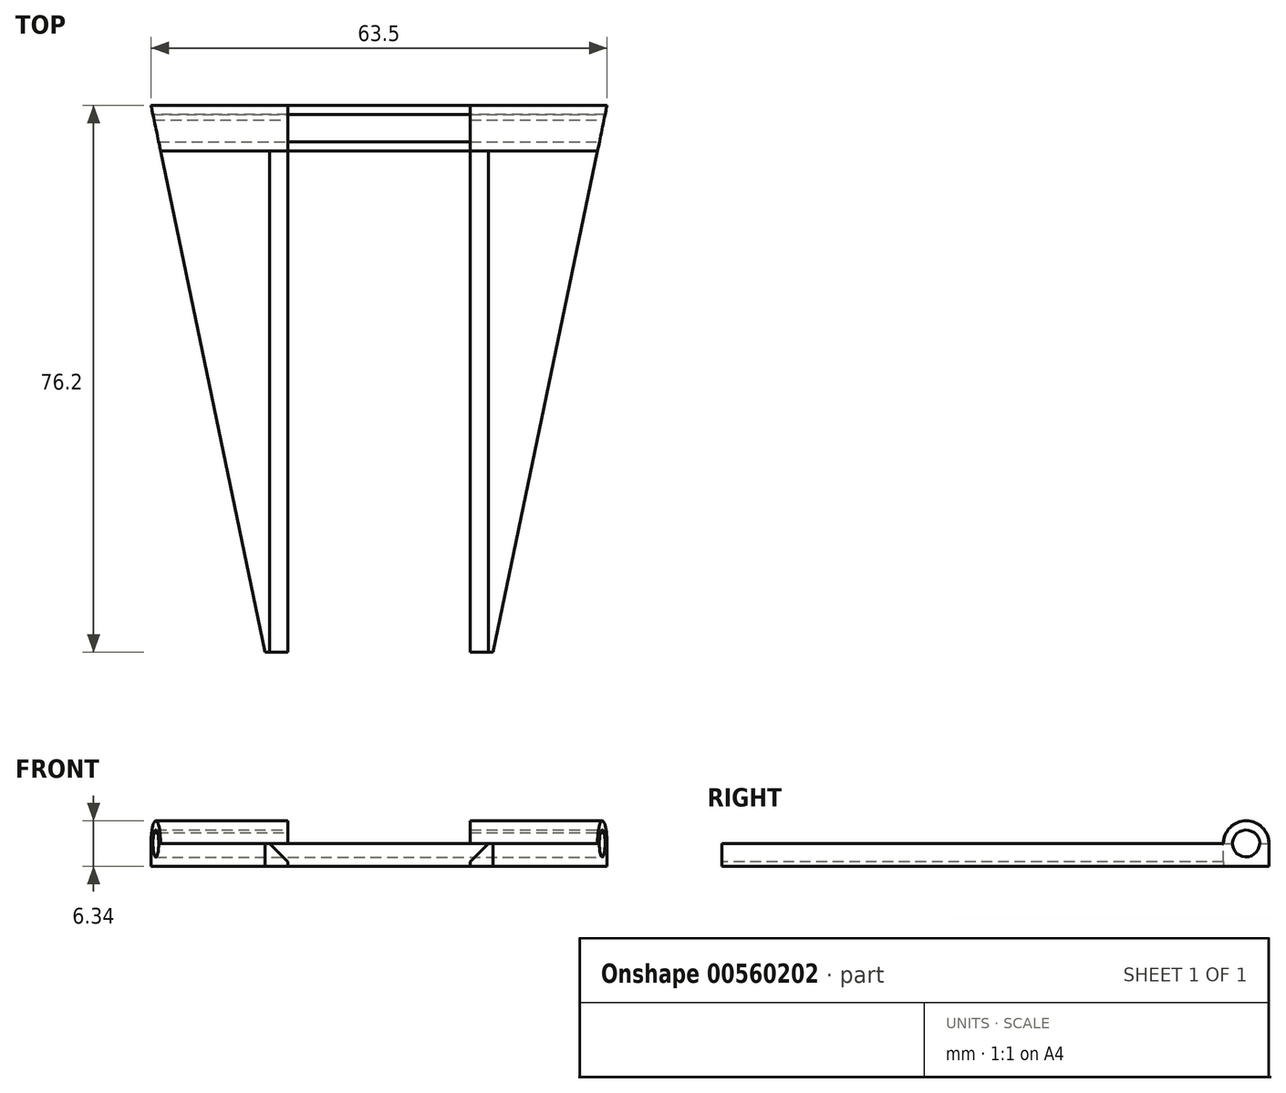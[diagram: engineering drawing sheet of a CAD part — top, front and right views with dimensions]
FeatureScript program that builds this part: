
annotation { "Feature Type Name" : "Feature", "Feature Type Description" : "" }
export const myFeature = defineFeature(function(context is Context, id is Id, definition is map)
    precondition{}
    {
        {
            var Q0;
            Q0=qCreatedBy(makeId("Top.planeOp"),FACE);
            var sketch = newSketch(context, id + "F0", { "sketchPlane" : qUnion([Q0])});
            skLineSegment(sketch, "E0", {"start": v(0, 0) * mm, "end": v(-38.1, 0) * mm});
            skLineSegment(sketch, "E1.MirrorCS", {"start": v(0, 0) * mm, "end": v(38.1, 0) * mm});
            skLineSegment(sketch, "E2", {"start": v(0, -76.2) * mm, "end": v(16.51, -76.2) * mm});
            skLineSegment(sketch, "E3.MirrorCS", {"start": v(0, -76.2) * mm, "end": v(-16.5, -76.2) * mm});
            skLineSegment(sketch, "E4", {"start": v(0, 0) * mm, "end": v(0, -76.2) * mm, "construction": true});
            skLineSegment(sketch, "E5", {"start": v(-38.1, 0) * mm, "end": v(-16.5, -76.2) * mm});
            skLineSegment(sketch, "E6", {"start": v(38.1, 0) * mm, "end": v(16.51, -76.2) * mm});
            skSolve(sketch);
        }
        {
            var Q0;
            Q0 = qSketchRegion(id + "F0", true);
            extrude(context, id + "F1", {"entities" : qUnion([Q0]), "depth" : 3.17 * mm, "offsetDistance" : 25.4 * mm});
        }
        {
            var Q0;
            Q0=qCreatedBy(makeId("Right.planeOp"),FACE);
            var sketch = newSketch(context, id + "F2", { "sketchPlane" : qUnion([Q0])});
            skArc(sketch, "E7", {"start": v(0, 3.16) * mm, "mid": v(-3.17, 6.34) * mm, "end": v(-6.35, 3.16) * mm});
            skLineSegment(sketch, "E8", {"start": v(-3.17, 3.16) * mm, "end": v(0, 3.16) * mm, "construction": true});
            skLineSegment(sketch, "E9", {"start": v(0, 3.16) * mm, "end": v(-3.17, 3.16) * mm});
            skLineSegment(sketch, "E10.MirrorCS", {"start": v(-6.35, 3.16) * mm, "end": v(-3.17, 3.16) * mm});
            skPoint(sketch, "E11.start.orphan", {"position": v(-3.17, -0.01) * mm});
            skArc(sketch, "E12.0", {"start": v(-1.27, 3.16) * mm, "mid": v(-3.17, 5.07) * mm, "end": v(-5.08, 3.16) * mm});
            skArc(sketch, "E13.MirrorCS", {"start": v(-1.27, 3.16) * mm, "mid": v(-3.17, 1.26) * mm, "end": v(-5.08, 3.16) * mm});
            skSolve(sketch);
        }
        {
            var Q0;
            {var subQ0=sQuery(id+"F2.wireOp",EDGE,"E7");Q0=makeQuery(id+"F2.imprint","IMPRINT",FACE,{"disambiguationData":[TD([[makeQuery(id+"F2.imprint","IMPRINT",EDGE,{"derivedFrom":subQ0}),1.0]])]});}
            extrude(context, id + "F3", {"entities" : qUnion([Q0]), "operationType" : NewBodyOperationType.ADD, "endBound" : BoundingType.SYMMETRIC, "depth" : 76.2 * mm, "offsetDistance" : 25.4 * mm});
        }
        {
            var Q0;
            Q0=qCreatedBy(makeId("Right.planeOp"),FACE);
            var sketch = newSketch(context, id + "F4", { "sketchPlane" : qUnion([Q0])});
            skCircle(sketch, "E14", {"center": v(-3.2, 3.18) * mm, "radius": 1.9 * mm});
            skSolve(sketch);
        }
        {
            var Q0;
            Q0 = qSketchRegion(id + "F4", true);
            extrude(context, id + "F5", {"entities" : qUnion([Q0]), "operationType" : NewBodyOperationType.REMOVE, "endBound" : BoundingType.SYMMETRIC, "oppositeDirection" : true, "depth" : 76.2 * mm, "offsetDistance" : 25.4 * mm});
        }
        {
            var Q0;
            Q0=qCreatedBy(makeId("Front.planeOp"),FACE);
            var sketch = newSketch(context, id + "F6", { "sketchPlane" : qUnion([Q0])});
            skLineSegment(sketch, "E15", {"start": v(0, 0) * mm, "end": v(0, 3.17) * mm});
            skLineSegment(sketch, "E16", {"start": v(0, 3.17) * mm, "end": v(12.7, 3.17) * mm});
            skLineSegment(sketch, "E17.MirrorCS", {"start": v(0, 3.17) * mm, "end": v(-12.7, 3.17) * mm});
            skLineSegment(sketch, "E18", {"start": v(12.7, 3.17) * mm, "end": v(12.7, 6.35) * mm});
            skLineSegment(sketch, "E19.MirrorCS", {"start": v(-12.7, 3.17) * mm, "end": v(-12.7, 6.35) * mm});
            skLineSegment(sketch, "E20", {"start": v(12.7, 6.35) * mm, "end": v(-12.7, 6.35) * mm});
            skSolve(sketch);
        }
        {
            var Q0;
            Q0 = qSketchRegion(id + "F6", true);
            extrude(context, id + "F7", {"entities" : qUnion([Q0]), "operationType" : NewBodyOperationType.REMOVE, "depth" : 12.7 * mm, "offsetDistance" : 25.4 * mm});
        }
        {
            var Q0;
            Q0=qCreatedBy(makeId("Top.planeOp"),FACE);
            var sketch = newSketch(context, id + "F8", { "sketchPlane" : qUnion([Q0])});
            skLineSegment(sketch, "E21", {"start": v(0, 0) * mm, "end": v(-31.75, 0) * mm});
            skLineSegment(sketch, "E22", {"start": v(-15.88, -76.2) * mm, "end": v(0, -76.2) * mm});
            skLineSegment(sketch, "E23", {"start": v(-31.75, 0) * mm, "end": v(-15.88, -76.2) * mm});
            skLineSegment(sketch, "E24.MirrorCS", {"start": v(15.88, -76.2) * mm, "end": v(0, -76.2) * mm});
            skLineSegment(sketch, "E25.MirrorCS", {"start": v(31.75, 0) * mm, "end": v(15.87, -76.2) * mm});
            skLineSegment(sketch, "E26.MirrorCS", {"start": v(0, 0) * mm, "end": v(31.75, 0) * mm});
            skSolve(sketch);
        }
        {
            var Q0;
            Q0=makeQuery(id+"F8.imprint","IMPRINT",FACE,{"disambiguationData":[TD([[makeQuery(id+"F8.imprint","IMPRINT",EDGE,{"derivedFrom":sQuery(id+"F8.wireOp",EDGE,"E21")}),1.0]])]});
            extrude(context, id + "F9", {"entities" : qUnion([Q0]), "operationType" : NewBodyOperationType.INTERSECT, "depth" : 25.4 * mm, "offsetDistance" : 25.4 * mm});
        }
        {
            var Q0;
            Q0=qCreatedBy(makeId("Right.planeOp"),FACE);
            var sketch = newSketch(context, id + "F10", { "sketchPlane" : qUnion([Q0])});
            skLineSegment(sketch, "E27", {"start": v(-28.96, 5.38) * mm, "end": v(-28.96, 2.84) * mm});
            skLineSegment(sketch, "E28", {"start": v(-28.96, 5.38) * mm, "end": v(-27.65, 5.38) * mm});
            skLineSegment(sketch, "E29", {"start": v(-27.65, 5.38) * mm, "end": v(-27.65, 2.84) * mm});
            skLineSegment(sketch, "E30", {"start": v(-27.65, 2.84) * mm, "end": v(-28.96, 2.84) * mm});
            skSolve(sketch);
        }
        {
            var Q0;
            Q0=makeQuery(id+"F10.imprint","IMPRINT",FACE,{"disambiguationData":[TD([[makeQuery(id+"F10.imprint","IMPRINT",EDGE,{"derivedFrom":sQuery(id+"F10.wireOp",EDGE,"E27")}),1.0]])]});
            extrude(context, id + "F11", {"entities" : qUnion([Q0]), "operationType" : NewBodyOperationType.ADD, "endBound" : BoundingType.SYMMETRIC, "depth" : 12.7 * mm, "offsetDistance" : 25.4 * mm});
        }
        {
            var Q0;
            Q0=qCreatedBy(makeId("Top.planeOp"),FACE);
            var sketch = newSketch(context, id + "F12", { "sketchPlane" : qUnion([Q0])});
            skLineSegment(sketch, "E31", {"start": v(-12.71, -6.35) * mm, "end": v(12.69, -6.35) * mm});
            skLineSegment(sketch, "E32", {"start": v(12.69, -6.35) * mm, "end": v(12.69, -80.87) * mm});
            skLineSegment(sketch, "E33", {"start": v(12.69, -80.87) * mm, "end": v(-12.71, -80.87) * mm});
            skLineSegment(sketch, "E34", {"start": v(-12.71, -6.35) * mm, "end": v(-12.71, -80.87) * mm});
            skSolve(sketch);
        }
        {
            var Q0;
            Q0 = qSketchRegion(id + "F12", true);
            extrude(context, id + "F13", {"entities" : qUnion([Q0]), "operationType" : NewBodyOperationType.REMOVE, "depth" : 12.7 * mm, "offsetDistance" : 25.4 * mm});
        }
        {
            var Q0;
            {var subQ0=sQuery(id+"F0.wireOp",EDGE,"E3.MirrorCS");var subQ1=sQuery(id+"F0.wireOp",EDGE,"E2");var subQ2=sQuery(id+"F0.wireOp",EDGE,"E5");var subQ3=sQuery(id+"F0.wireOp",EDGE,"E6");Q0=makeQuery(id+"F13.boolean.opBoolean","INTERSECT",EDGE,{"derivedFrom":[makeQuery(id+"F7.boolean.opBoolean","MERGE",FACE,{"derivedFrom":[makeQuery(id+"F3.boolean.opBoolean","SPLIT",FACE,{"disambiguationData":[TD([makeQuery(id+"F1.opExtrude","SWEPT_FACE",FACE,{"disambiguationData":[OSD([subQ1,subQ0])]})])],"derivedFrom":makeQuery(id+"F1.opExtrude","CAP_FACE",FACE,{"disambiguationData":[OSD([sQuery(id+"F0.wireOp",EDGE,"E0"),sQuery(id+"F0.wireOp",EDGE,"E1.MirrorCS"),subQ1,subQ0,subQ2,subQ3])],"isStart":false})}),makeQuery(id+"F7.opExtrude","SWEPT_FACE",FACE,{"disambiguationData":[OSD([sQuery(id+"F6.wireOp",EDGE,"E16"),sQuery(id+"F6.wireOp",EDGE,"E17.MirrorCS")])]})]}),makeQuery(id+"F13.opExtrude","SWEPT_FACE",FACE,{"disambiguationData":[OSD([sQuery(id+"F12.wireOp",EDGE,"E34")])]})]});}
            var Q1;
            {var subQ0=sQuery(id+"F0.wireOp",EDGE,"E3.MirrorCS");var subQ1=sQuery(id+"F0.wireOp",EDGE,"E2");var subQ2=sQuery(id+"F0.wireOp",EDGE,"E5");var subQ3=sQuery(id+"F0.wireOp",EDGE,"E6");Q1=makeQuery(id+"F13.boolean.opBoolean","INTERSECT",EDGE,{"derivedFrom":[makeQuery(id+"F7.boolean.opBoolean","MERGE",FACE,{"derivedFrom":[makeQuery(id+"F3.boolean.opBoolean","SPLIT",FACE,{"disambiguationData":[TD([makeQuery(id+"F1.opExtrude","SWEPT_FACE",FACE,{"disambiguationData":[OSD([subQ1,subQ0])]})])],"derivedFrom":makeQuery(id+"F1.opExtrude","CAP_FACE",FACE,{"disambiguationData":[OSD([sQuery(id+"F0.wireOp",EDGE,"E0"),sQuery(id+"F0.wireOp",EDGE,"E1.MirrorCS"),subQ1,subQ0,subQ2,subQ3])],"isStart":false})}),makeQuery(id+"F7.opExtrude","SWEPT_FACE",FACE,{"disambiguationData":[OSD([sQuery(id+"F6.wireOp",EDGE,"E16"),sQuery(id+"F6.wireOp",EDGE,"E17.MirrorCS")])]})]}),makeQuery(id+"F13.opExtrude","SWEPT_FACE",FACE,{"disambiguationData":[OSD([sQuery(id+"F12.wireOp",EDGE,"E32")])]})]});}
            chamfer(context, id + "F14", {"entities" : qUnion([Q0, Q1]), "width" : 2.54 * mm, "tangentPropagation" : true});
        }
    });
